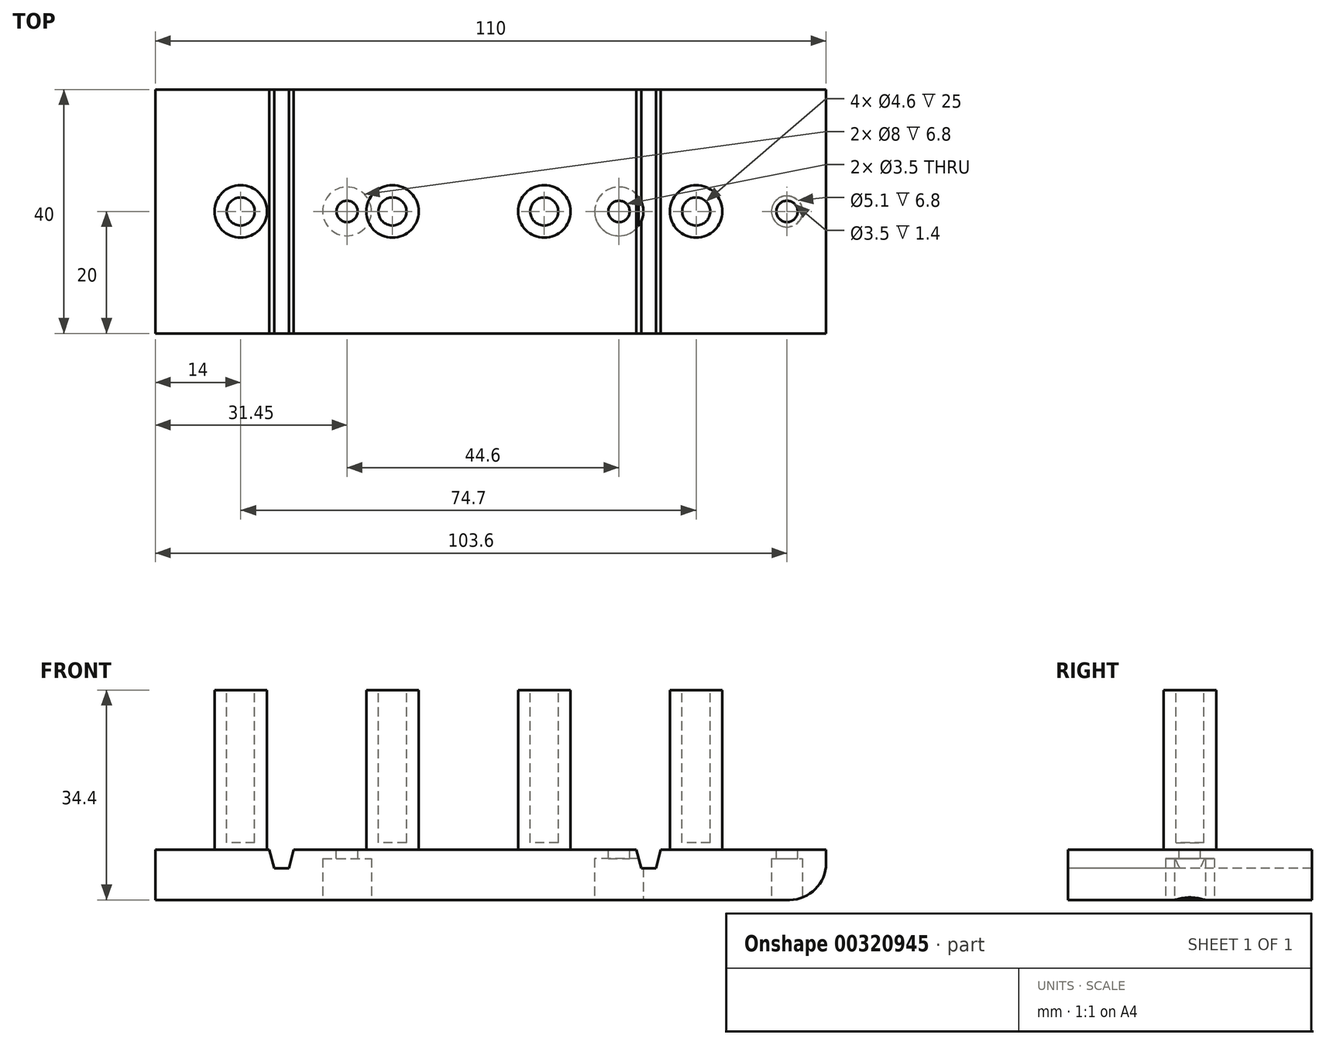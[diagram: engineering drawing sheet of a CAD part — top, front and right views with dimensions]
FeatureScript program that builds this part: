
annotation { "Feature Type Name" : "Feature", "Feature Type Description" : "" }
export const myFeature = defineFeature(function(context is Context, id is Id, definition is map)
    precondition{}
    {
        {
            var Q0;
            Q0=qCreatedBy(makeId("Top.planeOp"),FACE);
            var sketch = newSketch(context, id + "F0", { "sketchPlane" : qUnion([Q0])});
            skLineSegment(sketch, "E0.bottom", {"start": v(55, -20) * mm, "end": v(-55, -20) * mm});
            skLineSegment(sketch, "E0.top", {"start": v(55, 20) * mm, "end": v(-55, 20) * mm});
            skLineSegment(sketch, "E0.left", {"start": v(55, -20) * mm, "end": v(55, 20) * mm});
            skLineSegment(sketch, "E0.right", {"start": v(-55, -20) * mm, "end": v(-55, 20) * mm});
            skPoint(sketch, "E0.middle", {"position": v(0, 0) * mm});
            skSolve(sketch);
        }
        {
            var Q0;
            Q0 = qSketchRegion(id + "F0", true);
            extrude(context, id + "F1", {"entities" : qUnion([Q0]), "depth" : 8.2 * mm});
        }
        {
            var Q0;
            Q0=makeQuery(id+"F1.opExtrude","CAP_EDGE",EDGE,{"disambiguationData":[OSD([sQuery(id+"F0.wireOp",EDGE,"E0.left")])],"isStart":true});
            fillet(context, id + "F2", {"entities" : qUnion([Q0]), "radius" : 6 * mm, "tangentPropagation" : true, "allowEdgeOverflow" : false});
        }
        {
            var Q0;
            Q0=makeQuery(id+"F1.opExtrude","CAP_FACE",FACE,{"disambiguationData":[OSD([sQuery(id+"F0.wireOp",EDGE,"E0.bottom"),sQuery(id+"F0.wireOp",EDGE,"E0.top"),sQuery(id+"F0.wireOp",EDGE,"E0.left"),sQuery(id+"F0.wireOp",EDGE,"E0.right")])],"isStart":false});
            var sketch = newSketch(context, id + "F3", { "sketchPlane" : qUnion([Q0])});
            skCircle(sketch, "E1", {"center": v(-41, 0) * mm, "radius": 4.3 * mm});
            skCircle(sketch, "E2", {"center": v(-16.1, 0) * mm, "radius": 4.3 * mm});
            skCircle(sketch, "E3", {"center": v(8.8, 0) * mm, "radius": 4.3 * mm});
            skCircle(sketch, "E4", {"center": v(33.7, 0) * mm, "radius": 4.3 * mm});
            skSolve(sketch);
        }
        {
            var Q0;
            Q0 = qSketchRegion(id + "F3", true);
            extrude(context, id + "F4", {"entities" : qUnion([Q0]), "operationType" : NewBodyOperationType.ADD, "depth" : 26.2 * mm});
        }
        {
            var Q0;
            Q0=makeQuery(id+"F1.opExtrude","CAP_FACE",FACE,{"disambiguationData":[OSD([sQuery(id+"F0.wireOp",EDGE,"E0.bottom"),sQuery(id+"F0.wireOp",EDGE,"E0.top"),sQuery(id+"F0.wireOp",EDGE,"E0.left"),sQuery(id+"F0.wireOp",EDGE,"E0.right")])],"isStart":true});
            var sketch = newSketch(context, id + "F5", { "sketchPlane" : qUnion([Q0])});
            skCircle(sketch, "E5", {"center": v(48.6, 0) * mm, "radius": 2.55 * mm});
            skCircle(sketch, "E6", {"center": v(21.05, 0) * mm, "radius": 4 * mm});
            skCircle(sketch, "E7", {"center": v(-23.55, 0) * mm, "radius": 4 * mm});
            skSolve(sketch);
        }
        {
            var Q0;
            Q0 = qSketchRegion(id + "F5", true);
            extrude(context, id + "F6", {"entities" : qUnion([Q0]), "operationType" : NewBodyOperationType.REMOVE, "oppositeDirection" : true, "depth" : 6.8 * mm});
        }
        {
            var Q0;
            Q0=makeQuery(id+"F1.opExtrude","CAP_FACE",FACE,{"disambiguationData":[OSD([sQuery(id+"F0.wireOp",EDGE,"E0.bottom"),sQuery(id+"F0.wireOp",EDGE,"E0.top"),sQuery(id+"F0.wireOp",EDGE,"E0.left"),sQuery(id+"F0.wireOp",EDGE,"E0.right")])],"isStart":false});
            var sketch = newSketch(context, id + "F7", { "sketchPlane" : qUnion([Q0])});
            skCircle(sketch, "E8", {"center": v(48.6, 0) * mm, "radius": 1.75 * mm});
            skPoint(sketch, "E8.centerSnap0", {"position": v(55, 0) * mm});
            skCircle(sketch, "E9", {"center": v(21.05, 0) * mm, "radius": 1.75 * mm});
            skCircle(sketch, "E10", {"center": v(-23.55, 0) * mm, "radius": 1.75 * mm});
            skSolve(sketch);
        }
        {
            var Q0;
            Q0 = qSketchRegion(id + "F7", true);
            extrude(context, id + "F8", {"entities" : qUnion([Q0]), "operationType" : NewBodyOperationType.REMOVE, "endBound" : BoundingType.THROUGH_ALL, "oppositeDirection" : true, "depth" : 25 * mm});
        }
        {
            var Q0;
            Q0=makeQuery(id+"F1.opExtrude","SWEPT_FACE",FACE,{"disambiguationData":[OSD([sQuery(id+"F0.wireOp",EDGE,"E0.bottom")])]});
            var sketch = newSketch(context, id + "F9", { "sketchPlane" : qUnion([Q0])});
            skLineSegment(sketch, "E11", {"start": v(-36.3, 8.2) * mm, "end": v(-35.5, 5.2) * mm});
            skLineSegment(sketch, "E12", {"start": v(-35.5, 5.2) * mm, "end": v(-33.1, 5.2) * mm});
            skLineSegment(sketch, "E13", {"start": v(-33.1, 5.2) * mm, "end": v(-32.3, 8.2) * mm});
            skLineSegment(sketch, "E14", {"start": v(-36.3, 8.2) * mm, "end": v(-32.3, 8.2) * mm});
            skLineSegment(sketch, "E15", {"start": v(23.9, 8.2) * mm, "end": v(24.7, 5.2) * mm});
            skLineSegment(sketch, "E16", {"start": v(24.7, 5.2) * mm, "end": v(27.1, 5.2) * mm});
            skLineSegment(sketch, "E17", {"start": v(27.1, 5.2) * mm, "end": v(27.9, 8.2) * mm});
            skLineSegment(sketch, "E18", {"start": v(23.9, 8.2) * mm, "end": v(27.9, 8.2) * mm});
            skSolve(sketch);
        }
        {
            var Q0;
            Q0=makeQuery(id+"F9.imprint","IMPRINT",FACE,{"disambiguationData":[TD([[makeQuery(id+"F9.imprint","IMPRINT",EDGE,{"derivedFrom":sQuery(id+"F9.wireOp",EDGE,"E11")}),1.0]])]});
            var Q1;
            Q1=makeQuery(id+"F9.imprint","IMPRINT",FACE,{"disambiguationData":[TD([[makeQuery(id+"F9.imprint","IMPRINT",EDGE,{"derivedFrom":sQuery(id+"F9.wireOp",EDGE,"E15")}),1.0]])]});
            extrude(context, id + "F10", {"entities" : qUnion([Q0, Q1]), "operationType" : NewBodyOperationType.REMOVE, "endBound" : BoundingType.THROUGH_ALL, "oppositeDirection" : true, "depth" : 25 * mm});
        }
        {
            var Q0;
            Q0=makeQuery(id+"F4.opExtrude","CAP_FACE",FACE,{"disambiguationData":[OSD([sQuery(id+"F3.wireOp",EDGE,"E1")])],"isStart":false});
            var sketch = newSketch(context, id + "F11", { "sketchPlane" : qUnion([Q0])});
            skCircle(sketch, "E19", {"center": v(-41, 0) * mm, "radius": 2.3 * mm});
            skCircle(sketch, "E20", {"center": v(-16.1, 0) * mm, "radius": 2.3 * mm});
            skCircle(sketch, "E21", {"center": v(8.8, 0) * mm, "radius": 2.3 * mm});
            skCircle(sketch, "E22", {"center": v(33.7, 0) * mm, "radius": 2.3 * mm});
            skSolve(sketch);
        }
        {
            var Q0;
            Q0 = qSketchRegion(id + "F11", true);
            extrude(context, id + "F12", {"entities" : qUnion([Q0]), "operationType" : NewBodyOperationType.REMOVE, "oppositeDirection" : true, "depth" : 25 * mm});
        }
    });
